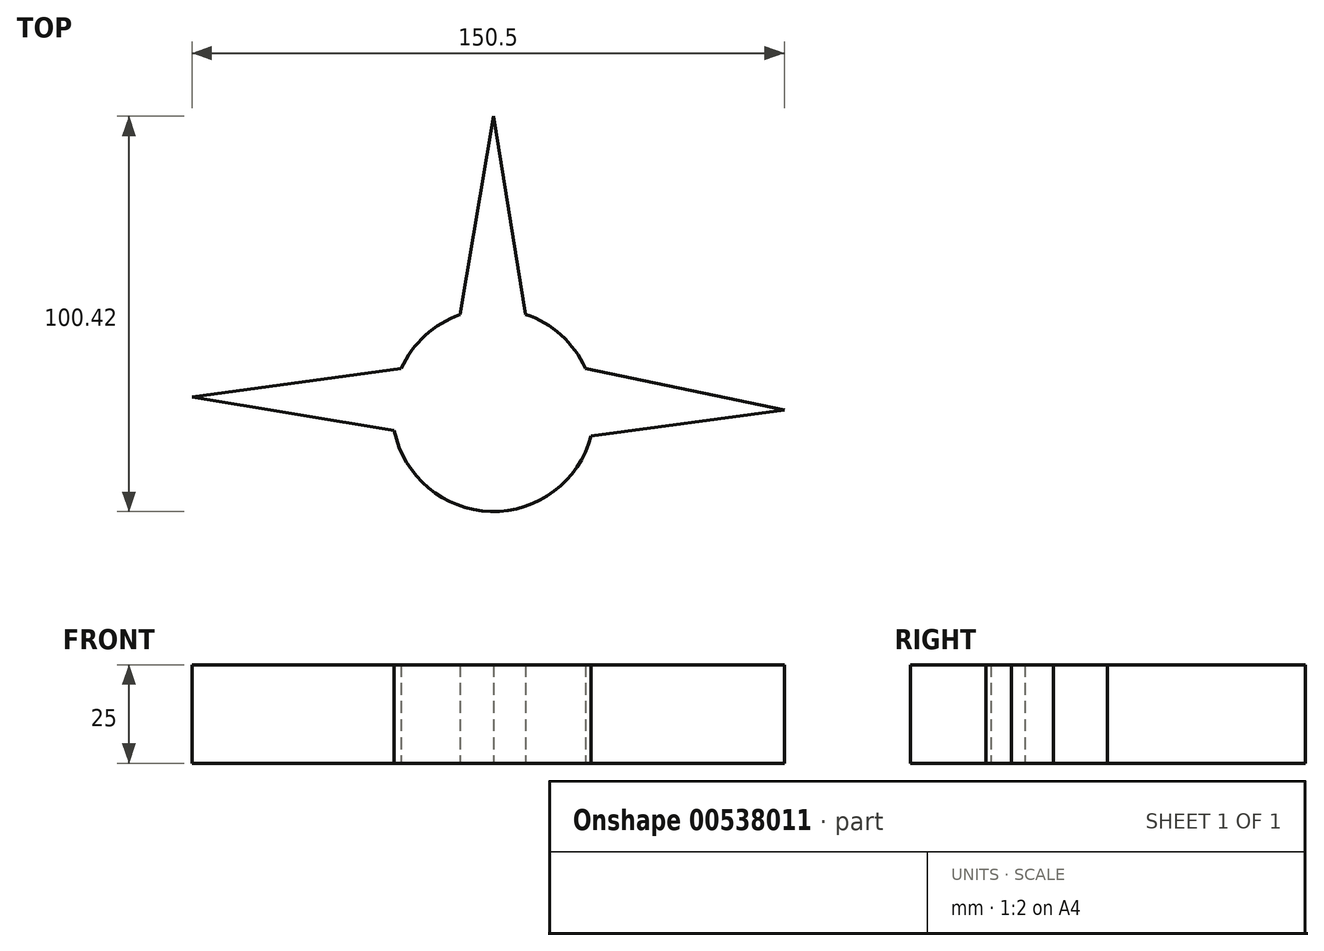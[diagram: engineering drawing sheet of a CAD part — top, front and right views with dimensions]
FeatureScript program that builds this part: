
annotation { "Feature Type Name" : "Feature", "Feature Type Description" : "" }
export const myFeature = defineFeature(function(context is Context, id is Id, definition is map)
    precondition{}
    {
        {
            var Q0;
            Q0=qCreatedBy(makeId("Top.planeOp"),FACE);
            var sketch = newSketch(context, id + "F0", { "sketchPlane" : qUnion([Q0])});
            skCircle(sketch, "E0", {"center": v(0, 0) * mm, "radius": 25.71 * mm});
            skLineSegment(sketch, "E1", {"start": v(-8.46, 24.28) * mm, "end": v(0, 74.7) * mm});
            skLineSegment(sketch, "E2", {"start": v(0, 74.7) * mm, "end": v(8.22, 24.36) * mm});
            skLineSegment(sketch, "E3", {"start": v(-25.18, -5.2) * mm, "end": v(-76.58, 3.38) * mm});
            skLineSegment(sketch, "E4", {"start": v(-76.58, 3.38) * mm, "end": v(-23.43, 10.58) * mm});
            skLineSegment(sketch, "E5", {"start": v(-8.5, -24.27) * mm, "end": v(-1.57, -75.37) * mm});
            skLineSegment(sketch, "E6", {"start": v(0, -75.37) * mm, "end": v(6.43, -24.9) * mm});
            skLineSegment(sketch, "E7", {"start": v(23.4, 10.66) * mm, "end": v(73.92, 0) * mm});
            skLineSegment(sketch, "E8", {"start": v(73.92, 0) * mm, "end": v(24.87, -6.52) * mm});
            skSolve(sketch);
        }
        {
            var Q0;
            {var subQ0=sQuery(id+"F0.wireOp",EDGE,"E0");var subQ6=makeQuery(id+"F0.imprint","IMPRINT",VERTEX,{"disambiguationData":[OD(0.0)],"derivedFrom":subQ0});Q0=makeQuery(id+"F0.imprint","IMPRINT",FACE,{"disambiguationData":[TD([[makeQuery(id+"F0.imprint","IMPRINT",EDGE,{"disambiguationData":[TD([[subQ6,-1.0]])],"derivedFrom":subQ0}),1.0]])]});}
            var Q1;
            {var subQ0=sQuery(id+"F0.wireOp",EDGE,"E1");Q1=makeQuery(id+"F0.imprint","IMPRINT",FACE,{"disambiguationData":[TD([[makeQuery(id+"F0.imprint","IMPRINT",EDGE,{"derivedFrom":subQ0}),-1.0]])]});}
            var Q2;
            {var subQ0=sQuery(id+"F0.wireOp",EDGE,"E3");Q2=makeQuery(id+"F0.imprint","IMPRINT",FACE,{"disambiguationData":[TD([[makeQuery(id+"F0.imprint","IMPRINT",EDGE,{"derivedFrom":subQ0}),-1.0]])]});}
            var Q3;
            {var subQ0=sQuery(id+"F0.wireOp",EDGE,"E7");Q3=makeQuery(id+"F0.imprint","IMPRINT",FACE,{"disambiguationData":[TD([[makeQuery(id+"F0.imprint","IMPRINT",EDGE,{"derivedFrom":subQ0}),-1.0]])]});}
            extrude(context, id + "F1", {"entities" : qUnion([Q0, Q1, Q2, Q3]), "depth" : 25 * mm, "offsetDistance" : 25 * mm});
        }
    });
